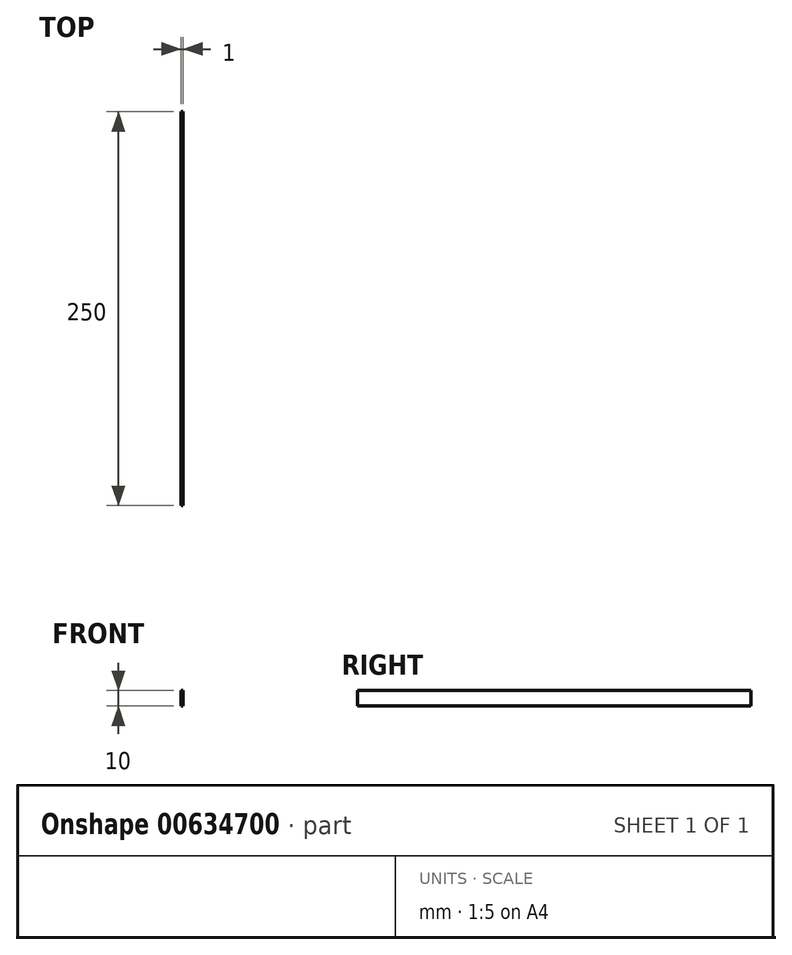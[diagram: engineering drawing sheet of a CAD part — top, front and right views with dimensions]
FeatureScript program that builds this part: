
annotation { "Feature Type Name" : "Feature", "Feature Type Description" : "" }
export const myFeature = defineFeature(function(context is Context, id is Id, definition is map)
    precondition{}
    {
        {
            var Q0;
            Q0=qCreatedBy(makeId("Right.planeOp"),FACE);
            var sketch = newSketch(context, id + "F0", { "sketchPlane" : qUnion([Q0])});
            skLineSegment(sketch, "E0.bottom", {"start": v(0, 0) * mm, "end": v(250, 0) * mm});
            skLineSegment(sketch, "E0.top", {"start": v(0, -10) * mm, "end": v(250, -10) * mm});
            skLineSegment(sketch, "E0.left", {"start": v(0, 0) * mm, "end": v(0, -10) * mm});
            skLineSegment(sketch, "E0.right", {"start": v(250, 0) * mm, "end": v(250, -10) * mm});
            skSolve(sketch);
        }
        {
            var Q0;
            Q0 = qSketchRegion(id + "F0", true);
            extrude(context, id + "F1", {"entities" : qUnion([Q0]), "depth" : 1 * mm, "offsetDistance" : 25 * mm});
        }
    });
